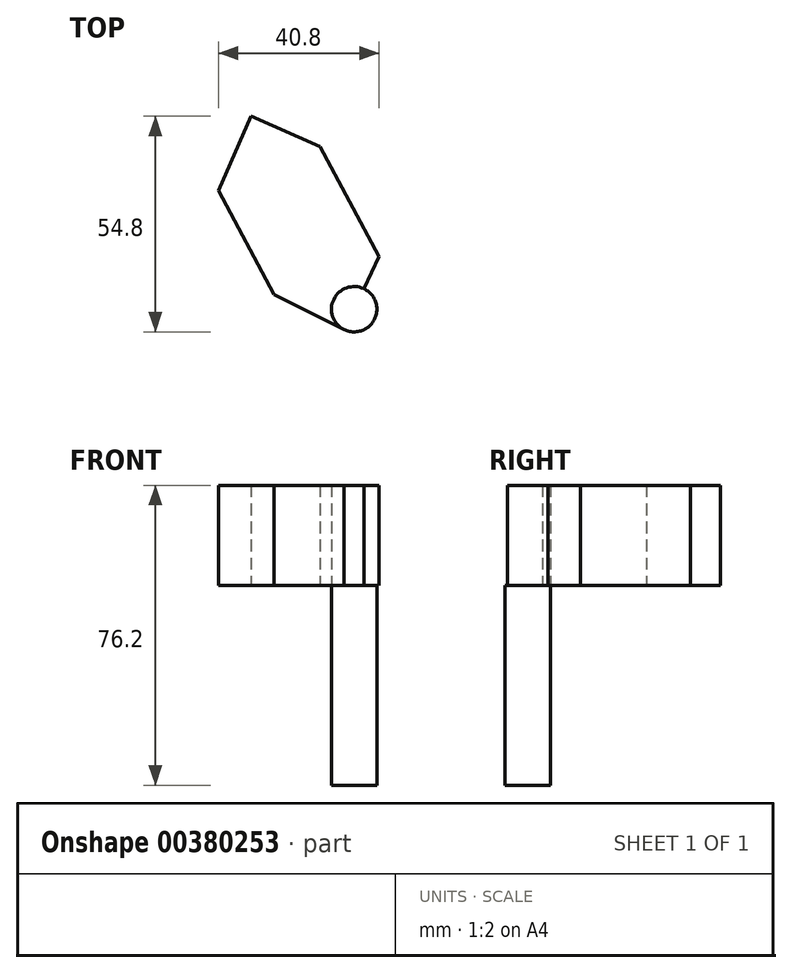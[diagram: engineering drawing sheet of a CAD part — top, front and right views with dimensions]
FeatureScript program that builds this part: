
annotation { "Feature Type Name" : "Feature", "Feature Type Description" : "" }
export const myFeature = defineFeature(function(context is Context, id is Id, definition is map)
    precondition{}
    {
        {
            var Q0;
            Q0=qCreatedBy(makeId("Top.planeOp"),FACE);
            var sketch = newSketch(context, id + "F0", { "sketchPlane" : qUnion([Q0])});
            skCircle(sketch, "E0", {"center": v(-48.73, -41.33) * mm, "radius": 5.76 * mm});
            skSolve(sketch);
        }
        {
            var Q0;
            Q0=makeQuery(id+"F0.imprint","IMPRINT",FACE,{"disambiguationData":[TD([[makeQuery(id+"F0.imprint","IMPRINT",EDGE,{"derivedFrom":sQuery(id+"F0.wireOp",EDGE,"E0")}),1.0]])]});
            extrude(context, id + "F1", {"entities" : qUnion([Q0]), "depth" : 50.8 * mm});
        }
        {
            var Q0;
            Q0=makeQuery(id+"F1.opExtrude","CAP_FACE",FACE,{"disambiguationData":[OSD([sQuery(id+"F0.wireOp",EDGE,"E0")])],"isStart":false});
            var sketch = newSketch(context, id + "F2", { "sketchPlane" : qUnion([Q0])});
            skLineSegment(sketch, "E1", {"start": v(-48.73, -41.33) * mm, "end": v(-42.43, -27.94) * mm});
            skLineSegment(sketch, "E2", {"start": v(-42.43, -27.94) * mm, "end": v(-57.39, 0) * mm});
            skLineSegment(sketch, "E3", {"start": v(-57.39, 0) * mm, "end": v(-74.98, 7.71) * mm});
            skLineSegment(sketch, "E4", {"start": v(-74.98, 7.71) * mm, "end": v(-83.23, -11.13) * mm});
            skLineSegment(sketch, "E5", {"start": v(-83.23, -11.13) * mm, "end": v(-69.06, -37.54) * mm});
            skLineSegment(sketch, "E6", {"start": v(-69.06, -37.54) * mm, "end": v(-51.32, -46.47) * mm});
            skLineSegment(sketch, "E7", {"start": v(-51.32, -46.47) * mm, "end": v(-48.73, -41.33) * mm});
            skSolve(sketch);
        }
        {
            var Q0;
            {var subQ0=sQuery(id+"F2.wireOp",EDGE,"E2");Q0=makeQuery(id+"F2.imprint","IMPRINT",FACE,{"disambiguationData":[TD([[makeQuery(id+"F2.imprint","IMPRINT",EDGE,{"derivedFrom":subQ0}),1.0]])]});}
            extrude(context, id + "F3", {"entities" : qUnion([Q0]), "depth" : 25.4 * mm});
        }
    });
